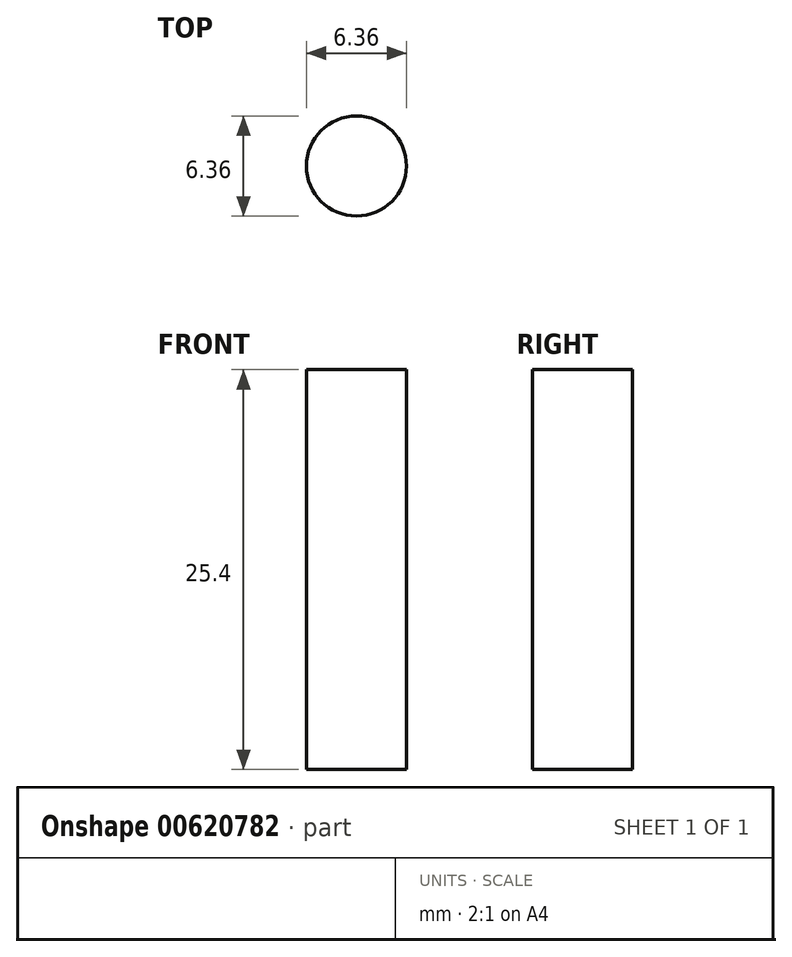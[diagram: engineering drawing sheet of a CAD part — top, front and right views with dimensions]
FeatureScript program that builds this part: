
annotation { "Feature Type Name" : "Feature", "Feature Type Description" : "" }
export const myFeature = defineFeature(function(context is Context, id is Id, definition is map)
    precondition{}
    {
        {
            var Q0;
            Q0=qCreatedBy(makeId("Top.planeOp"),FACE);
            var sketch = newSketch(context, id + "F0", { "sketchPlane" : qUnion([Q0])});
            skCircle(sketch, "E0", {"center": v(0, 0) * mm, "radius": 3.18 * mm});
            skSolve(sketch);
        }
        {
            var Q0;
            Q0 = qSketchRegion(id + "F0", true);
            extrude(context, id + "F1", {"entities" : qUnion([Q0]), "depth" : 12.7 * mm, "offsetDistance" : 25 * mm, "hasSecondDirection" : true, "secondDirectionOppositeDirection" : true, "secondDirectionDepth" : 12.7 * mm});
        }
    });
